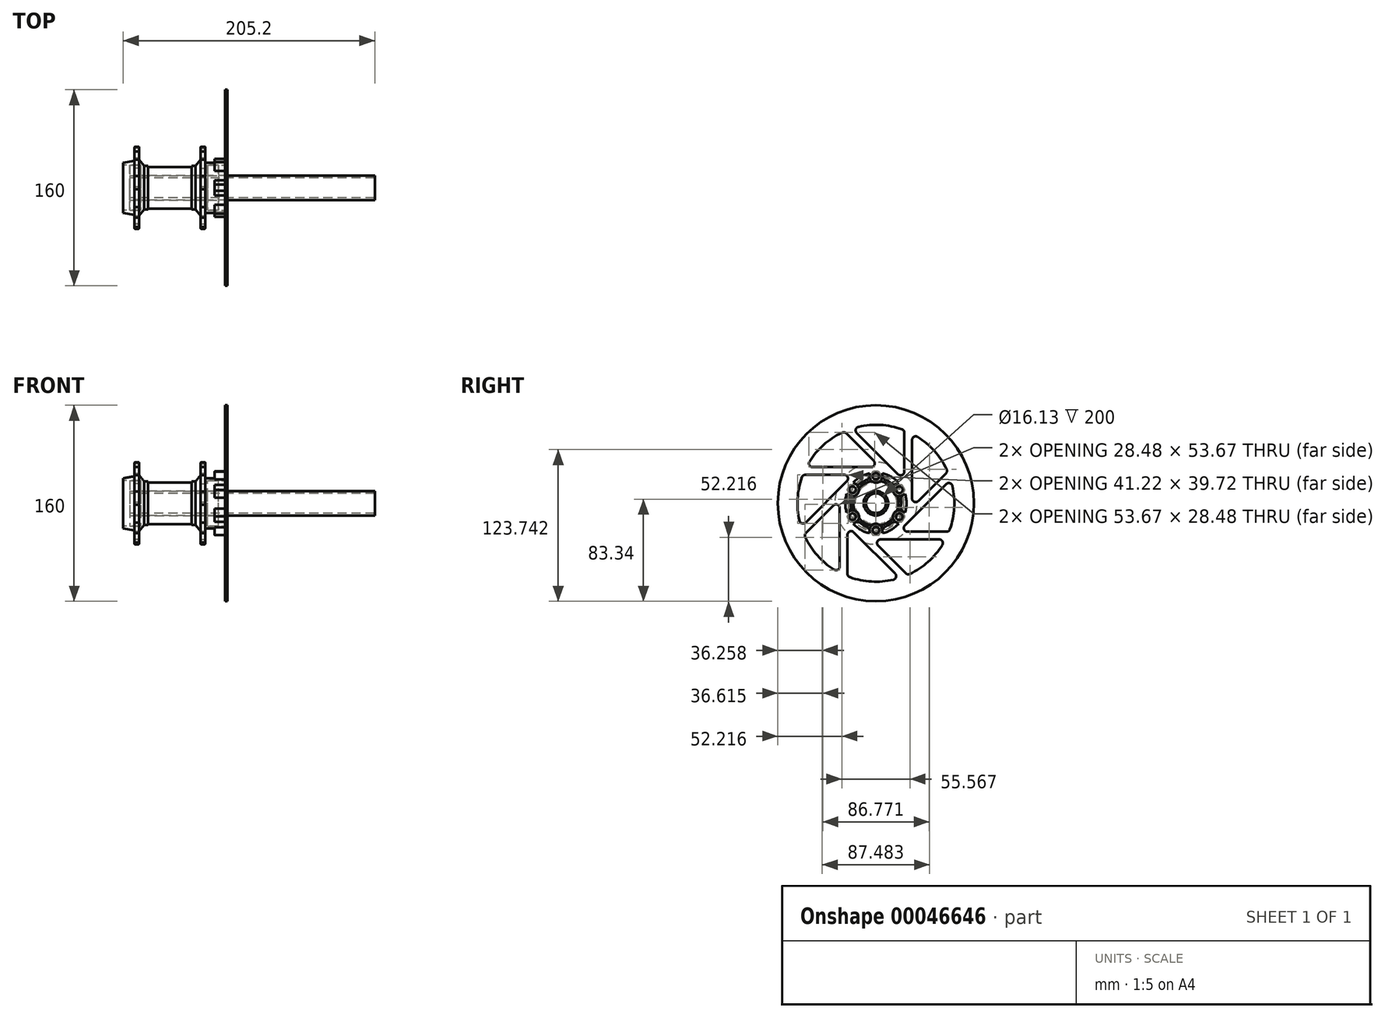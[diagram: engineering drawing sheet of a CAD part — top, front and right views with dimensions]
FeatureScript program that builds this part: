
annotation { "Feature Type Name" : "Feature", "Feature Type Description" : "" }
export const myFeature = defineFeature(function(context is Context, id is Id, definition is map)
    precondition{}
    {
        {
            var Q0;
            Q0=qCreatedBy(makeId("Front.planeOp"),FACE);
            var sketch = newSketch(context, id + "F0", { "sketchPlane" : qUnion([Q0])});
            skLineSegment(sketch, "E0", {"start": v(0, 0) * mm, "end": v(29, 0) * mm});
            skLineSegment(sketch, "E1", {"start": v(29, 0) * mm, "end": v(29, 33.5) * mm});
            skLineSegment(sketch, "E2", {"start": v(29, 33.5) * mm, "end": v(25, 33.5) * mm});
            skLineSegment(sketch, "E3", {"start": v(25, 33.5) * mm, "end": v(25, 17.85) * mm});
            skLineSegment(sketch, "E4", {"start": v(25, 17.85) * mm, "end": v(17.7, 17.85) * mm});
            skLineSegment(sketch, "E5", {"start": v(17.7, 17.85) * mm, "end": v(17.7, 17) * mm});
            skLineSegment(sketch, "E6", {"start": v(17.7, 17) * mm, "end": v(0, 17) * mm});
            skLineSegment(sketch, "E7", {"start": v(0, 17) * mm, "end": v(0, 0) * mm});
            skLineSegment(sketch, "E8", {"start": v(0, 0) * mm, "end": v(0, -15.6) * mm, "construction": true});
            skLineSegment(sketch, "E9", {"start": v(0, 0) * mm, "end": v(-20.97, 0) * mm, "construction": true});
            skSolve(sketch);
        }
        {
            var Q0;
            Q0 = qSketchRegion(id + "F0", true);
            var Q1;
            Q1=sQuery(id+"F0.wireOp",EDGE,"E9");
            revolve(context, id + "F1", {"entities" : qUnion([Q0]), "axis" : qUnion([Q1]), "revolveType" : RevolveType.FULL});
        }
        {
            var Q0;
            Q0=makeQuery(id+"F1.opRevolve","SWEPT_EDGE",EDGE,{"disambiguationData":[OSD([sQuery(id+"F0.wireOp",EDGE,"E3"),sQuery(id+"F0.wireOp",EDGE,"E4")])]});
            chamfer(context, id + "F2", {"entities" : qUnion([Q0]), "chamferType" : ChamferType.TWO_OFFSETS, "width1" : 5 * mm, "oppositeDirection" : false, "width2" : 4 * mm, "tangentPropagation" : true});
        }
        {
            var Q0;
            Q0=makeQuery(id+"F1.opRevolve","SWEPT_EDGE",EDGE,{"disambiguationData":[OSD([sQuery(id+"F0.wireOp",EDGE,"E2"),sQuery(id+"F0.wireOp",EDGE,"E3")])]});
            var Q1;
            Q1=makeQuery(id+"F1.opRevolve","SWEPT_EDGE",EDGE,{"disambiguationData":[OSD([sQuery(id+"F0.wireOp",EDGE,"E1"),sQuery(id+"F0.wireOp",EDGE,"E2")])]});
            fillet(context, id + "F3", {"entities" : qUnion([Q0, Q1]), "radius" : .8 * mm, "tangentPropagation" : true, "allowEdgeOverflow" : false});
        }
        {
            var Q0;
            Q0=makeQuery(id+"F1.opRevolve","SWEPT_BODY",BODY,{"disambiguationData":[OSD([sQuery(id+"F0.wireOp",EDGE,"E0"),sQuery(id+"F0.wireOp",EDGE,"E1"),sQuery(id+"F0.wireOp",EDGE,"E2"),sQuery(id+"F0.wireOp",EDGE,"E3"),sQuery(id+"F0.wireOp",EDGE,"E4"),sQuery(id+"F0.wireOp",EDGE,"E5"),sQuery(id+"F0.wireOp",EDGE,"E6"),sQuery(id+"F0.wireOp",EDGE,"E7")])]});
            var Q1;
            Q1=makeQuery(id+"F1.opRevolve","SWEPT_FACE",FACE,{"disambiguationData":[OSD([sQuery(id+"F0.wireOp",EDGE,"E7")])]});
            mirror(context, id + "F4", {"operationType" : NewBodyOperationType.ADD, "entities" : qUnion([Q0]), "mirrorPlane" : qUnion([Q1])});
        }
        {
            var Q0;
            Q0=makeQuery(id+"F1.opRevolve","SWEPT_FACE",FACE,{"disambiguationData":[OSD([sQuery(id+"F0.wireOp",EDGE,"E1")])]});
            var sketch = newSketch(context, id + "F5", { "sketchPlane" : qUnion([Q0])});
            skCircle(sketch, "E10", {"center": v(0, 0) * mm, "radius": 20.5 * mm});
            skSolve(sketch);
        }
        {
            var Q0;
            Q0 = qSketchRegion(id + "F5", true);
            extrude(context, id + "F6", {"entities" : qUnion([Q0]), "operationType" : NewBodyOperationType.ADD, "depth" : 16 * mm});
        }
        {
            var Q0;
            Q0=makeQuery(id+"F6.opExtrude","CAP_FACE",FACE,{"disambiguationData":[OSD([sQuery(id+"F5.wireOp",EDGE,"E10")])],"isStart":false});
            var sketch = newSketch(context, id + "F7", { "sketchPlane" : qUnion([Q0])});
            skArc(sketch, "E11", {"start": v(2.5, 25.88) * mm, "mid": v(0, 26) * mm, "end": v(-2.5, 25.88) * mm});
            skLineSegment(sketch, "E12", {"start": v(-2.5, 25.88) * mm, "end": v(-17.44, 0) * mm});
            skLineSegment(sketch, "E13", {"start": v(-17.44, 0) * mm, "end": v(17.44, 0) * mm});
            skLineSegment(sketch, "E14", {"start": v(17.44, 0) * mm, "end": v(2.5, 25.88) * mm});
            skLineSegment(sketch, "E15", {"start": v(0, 0) * mm, "end": v(0, 26) * mm, "construction": true});
            skCircle(sketch, "E16", {"center": v(0, 22) * mm, "radius": 2.5 * mm, "construction": true});
            skSolve(sketch);
        }
        {
            var Q0;
            Q0 = qSketchRegion(id + "F7", true);
            extrude(context, id + "F8", {"entities" : qUnion([Q0]), "operationType" : NewBodyOperationType.ADD, "oppositeDirection" : true, "depth" : 8.5 * mm});
        }
        {
            var Q0;
            Q0=makeQuery(id+"F8.opExtrude","SWEPT_BODY",BODY,{"disambiguationData":[OSD([sQuery(id+"F7.wireOp",EDGE,"E11"),sQuery(id+"F7.wireOp",EDGE,"E12"),sQuery(id+"F7.wireOp",EDGE,"E13"),sQuery(id+"F7.wireOp",EDGE,"E14")])]});
            var Q1;
            Q1=makeQuery(id+"F8.opExtrude","SWEPT_FACE",FACE,{"disambiguationData":[OSD([sQuery(id+"F7.wireOp",EDGE,"E12")])]});
            var Q2;
            Q2=makeQuery(id+"F8.opExtrude","SWEPT_FACE",FACE,{"disambiguationData":[OSD([sQuery(id+"F7.wireOp",EDGE,"E11")])]});
            var Q3;
            Q3=makeQuery(id+"F8.opExtrude","CAP_FACE",FACE,{"disambiguationData":[OSD([sQuery(id+"F7.wireOp",EDGE,"E11"),sQuery(id+"F7.wireOp",EDGE,"E12"),sQuery(id+"F7.wireOp",EDGE,"E13"),sQuery(id+"F7.wireOp",EDGE,"E14")])],"isStart":false});
            var Q4;
            Q4=makeQuery(id+"F8.opExtrude","SWEPT_FACE",FACE,{"disambiguationData":[OSD([sQuery(id+"F7.wireOp",EDGE,"E14")])]});
            var Q5;
            Q5=sQuery(id+"F0.wireOp",EDGE,"E0");
            circularPattern(context, id + "F9", {"operationType" : NewBodyOperationType.ADD, "faces" : qUnion([Q1, Q2, Q3, Q4]), "axis" : qUnion([Q5]), "angle" : 360 * degree, "instanceCount" : 6, "equalSpace" : true, "patternType" : PatternType.FACE});
        }
        {
            var Q0;
            Q0=makeQuery(id+"F8.boolean.opBoolean","MERGE",FACE,{"derivedFrom":[makeQuery(id+"F6.opExtrude","CAP_FACE",FACE,{"disambiguationData":[OSD([sQuery(id+"F5.wireOp",EDGE,"E10")])],"isStart":false}),makeQuery(id+"F8.opExtrude","CAP_FACE",FACE,{"disambiguationData":[OSD([sQuery(id+"F7.wireOp",EDGE,"E11"),sQuery(id+"F7.wireOp",EDGE,"E12"),sQuery(id+"F7.wireOp",EDGE,"E13"),sQuery(id+"F7.wireOp",EDGE,"E14")])],"isStart":true})]});
            var sketch = newSketch(context, id + "F10", { "sketchPlane" : qUnion([Q0])});
            skCircle(sketch, "E17", {"center": v(0, 0) * mm, "radius": 18.5 * mm});
            skSolve(sketch);
        }
        {
            var Q0;
            Q0 = qSketchRegion(id + "F10", true);
            extrude(context, id + "F11", {"entities" : qUnion([Q0]), "operationType" : NewBodyOperationType.REMOVE, "oppositeDirection" : true, "depth" : 14.2 * mm});
        }
        {
            var Q0;
            Q0=makeQuery(id+"F11.boolean.opBoolean","COPY",FACE,{"derivedFrom":makeQuery(id+"F11.opExtrude","CAP_FACE",FACE,{"disambiguationData":[OSD([sQuery(id+"F10.wireOp",EDGE,"E17")])],"isStart":false})});
            extrude(context, id + "F12", {"entities" : qUnion([Q0]), "depth" : 9 * mm});
        }
        {
            var Q0;
            Q0=makeQuery(id+"F4.opPattern","COPY",FACE,{"derivedFrom":makeQuery(id+"F1.opRevolve","SWEPT_FACE",FACE,{"disambiguationData":[OSD([sQuery(id+"F0.wireOp",EDGE,"E1")])]}),"instanceName":"1"});
            var sketch = newSketch(context, id + "F13", { "sketchPlane" : qUnion([Q0])});
            skCircle(sketch, "E18", {"center": v(0, 0) * mm, "radius": 22 * mm});
            skSolve(sketch);
        }
        {
            var Q0;
            Q0 = qSketchRegion(id + "F13", true);
            extrude(context, id + "F14", {"entities" : qUnion([Q0]), "operationType" : NewBodyOperationType.ADD, "depth" : 9 * mm, "hasDraft" : true, "draftAngle" : 10 * degree, "draftPullDirection" : true});
        }
        {
            var Q0;
            Q0=makeQuery(id+"F14.opExtrude","CAP_FACE",FACE,{"disambiguationData":[OSD([sQuery(id+"F13.wireOp",EDGE,"E18")])],"isStart":false});
            var sketch = newSketch(context, id + "F15", { "sketchPlane" : qUnion([Q0])});
            skCircle(sketch, "E19", {"center": v(0, 0) * mm, "radius": 18.5 * mm});
            skSolve(sketch);
        }
        {
            var Q0;
            Q0 = qSketchRegion(id + "F15", true);
            extrude(context, id + "F16", {"entities" : qUnion([Q0]), "operationType" : NewBodyOperationType.REMOVE, "oppositeDirection" : true, "depth" : 14.2 * mm});
        }
        {
            var Q0;
            Q0=makeQuery(id+"F16.boolean.opBoolean","COPY",FACE,{"derivedFrom":makeQuery(id+"F16.opExtrude","CAP_FACE",FACE,{"disambiguationData":[OSD([sQuery(id+"F15.wireOp",EDGE,"E19")])],"isStart":false})});
            extrude(context, id + "F17", {"entities" : qUnion([Q0]), "depth" : 9 * mm});
        }
        {
            var Q0;
            Q0=qCreatedBy(makeId("Right.planeOp"),FACE);
            var sketch = newSketch(context, id + "F18", { "sketchPlane" : qUnion([Q0])});
            skCircle(sketch, "E20", {"center": v(0, 0) * mm, "radius": 10 * mm});
            skSolve(sketch);
        }
        {
            var Q0;
            Q0 = qSketchRegion(id + "F18", true);
            extrude(context, id + "F19", {"entities" : qUnion([Q0]), "operationType" : NewBodyOperationType.REMOVE, "endBound" : BoundingType.THROUGH_ALL, "oppositeDirection" : true, "depth" : 25 * mm, "hasSecondDirection" : true, "secondDirectionBound" : SecondDirectionBoundingType.THROUGH_ALL, "secondDirectionOppositeDirection" : false, "secondDirectionDepth" : 25 * mm});
        }
        {
            var Q0;
            Q0=makeQuery(id+"F8.boolean.opBoolean","MERGE",FACE,{"derivedFrom":[makeQuery(id+"F6.opExtrude","CAP_FACE",FACE,{"disambiguationData":[OSD([sQuery(id+"F5.wireOp",EDGE,"E10")])],"isStart":false}),makeQuery(id+"F8.opExtrude","CAP_FACE",FACE,{"disambiguationData":[OSD([sQuery(id+"F7.wireOp",EDGE,"E11"),sQuery(id+"F7.wireOp",EDGE,"E12"),sQuery(id+"F7.wireOp",EDGE,"E13"),sQuery(id+"F7.wireOp",EDGE,"E14")])],"isStart":true})]});
            var sketch = newSketch(context, id + "F20", { "sketchPlane" : qUnion([Q0])});
            skArc(sketch, "E21", {"start": v(-5.25, 24.44) * mm, "mid": v(-8.98, 23.33) * mm, "end": v(-12.5, 21.65) * mm});
            skCircle(sketch, "E22", {"center": v(0, 22) * mm, "radius": 2.7 * mm});
            skArc(sketch, "E23", {"start": v(-5.25, 22) * mm, "mid": v(0, 16.75) * mm, "end": v(5.25, 22) * mm});
            skLineSegment(sketch, "E24", {"start": v(-5.25, 22) * mm, "end": v(-5.25, 24.44) * mm});
            skLineSegment(sketch, "E25", {"start": v(5.25, 22) * mm, "end": v(5.25, 24.44) * mm});
            skLineSegment(sketch, "E26", {"start": v(-40, 69.28) * mm, "end": v(-12.5, 21.65) * mm});
            skLineSegment(sketch, "E27", {"start": v(40, 69.28) * mm, "end": v(12.5, 21.65) * mm});
            skArc(sketch, "E28", {"start": v(40, 69.28) * mm, "mid": v(0, 80) * mm, "end": v(-40, 69.28) * mm});
            skArc(sketch, "E29.trimOffspring", {"start": v(12.5, 21.65) * mm, "mid": v(8.98, 23.33) * mm, "end": v(5.25, 24.44) * mm});
            skSolve(sketch);
        }
        {
            var Q0;
            Q0 = qSketchRegion(id + "F20", true);
            extrude(context, id + "F21", {"entities" : qUnion([Q0]), "depth" : 2 * mm});
        }
        {
            var Q0;
            Q0=makeQuery(id+"F21.opExtrude","SWEPT_BODY",BODY,{"disambiguationData":[OSD([sQuery(id+"F20.wireOp",EDGE,"E21"),sQuery(id+"F20.wireOp",EDGE,"E22"),sQuery(id+"F20.wireOp",EDGE,"E23"),sQuery(id+"F20.wireOp",EDGE,"E24"),sQuery(id+"F20.wireOp",EDGE,"E25"),sQuery(id+"F20.wireOp",EDGE,"E26"),sQuery(id+"F20.wireOp",EDGE,"E27"),sQuery(id+"F20.wireOp",EDGE,"E28"),sQuery(id+"F20.wireOp",EDGE,"E29.trimOffspring")])]});
            var Q1;
            Q1=sQuery(id+"F0.wireOp",EDGE,"E0");
            circularPattern(context, id + "F22", {"operationType" : NewBodyOperationType.ADD, "entities" : qUnion([Q0]), "axis" : qUnion([Q1]), "angle" : 360 * degree, "instanceCount" : 6, "equalSpace" : true});
        }
        {
            var Q0;
            {var subQ0=makeQuery(id+"F21.opExtrude","CAP_FACE",FACE,{"disambiguationData":[OSD([sQuery(id+"F20.wireOp",EDGE,"E21"),sQuery(id+"F20.wireOp",EDGE,"E22"),sQuery(id+"F20.wireOp",EDGE,"E23"),sQuery(id+"F20.wireOp",EDGE,"E24"),sQuery(id+"F20.wireOp",EDGE,"E25"),sQuery(id+"F20.wireOp",EDGE,"E26"),sQuery(id+"F20.wireOp",EDGE,"E27"),sQuery(id+"F20.wireOp",EDGE,"E28"),sQuery(id+"F20.wireOp",EDGE,"E29.trimOffspring")])],"isStart":false});Q0=makeQuery(id+"F22.boolean.opBoolean","MERGE",FACE,{"derivedFrom":[subQ0,makeQuery(id+"F22.opPattern","COPY",FACE,{"derivedFrom":subQ0,"instanceName":"1"}),makeQuery(id+"F22.opPattern","COPY",FACE,{"derivedFrom":subQ0,"instanceName":"2"}),makeQuery(id+"F22.opPattern","COPY",FACE,{"derivedFrom":subQ0,"instanceName":"3"}),makeQuery(id+"F22.opPattern","COPY",FACE,{"derivedFrom":subQ0,"instanceName":"4"}),makeQuery(id+"F22.opPattern","COPY",FACE,{"derivedFrom":subQ0,"instanceName":"5"})]});}
            var sketch = newSketch(context, id + "F23", { "sketchPlane" : qUnion([Q0])});
            skLineSegment(sketch, "E30", {"start": v(-51.62, 29.5) * mm, "end": v(-3.93, 29.5) * mm});
            skLineSegment(sketch, "E31", {"start": v(-1.81, 34.62) * mm, "end": v(-24.3, 57.1) * mm});
            skArc(sketch, "E32", {"start": v(-27.72, 57.69) * mm, "mid": v(-42.6, 47.76) * mm, "end": v(-54.16, 34.1) * mm});
            skPoint(sketch, "E33.visualSharp", {"position": v(3.3, 29.5) * mm});
            skArc(sketch, "E33.filletArc", {"start": v(-3.93, 29.5) * mm, "mid": v(-1.16, 31.35) * mm, "end": v(-1.81, 34.62) * mm});
            skPoint(sketch, "E34.visualSharp", {"position": v(-25.77, 58.58) * mm});
            skArc(sketch, "E34.filletArc", {"start": v(-24.3, 57.1) * mm, "mid": v(-25.91, 57.94) * mm, "end": v(-27.72, 57.69) * mm});
            skPoint(sketch, "E35.visualSharp", {"position": v(-56.8, 29.5) * mm});
            skArc(sketch, "E35.filletArc", {"start": v(-54.16, 34.1) * mm, "mid": v(-54.25, 31.05) * mm, "end": v(-51.62, 29.5) * mm});
            skSolve(sketch);
        }
        {
            var Q0;
            Q0 = qSketchRegion(id + "F23", true);
            extrude(context, id + "F24", {"entities" : qUnion([Q0]), "operationType" : NewBodyOperationType.REMOVE, "endBound" : BoundingType.THROUGH_ALL, "oppositeDirection" : true, "depth" : 25 * mm});
        }
        {
            var Q0;
            Q0=makeQuery(id+"F24.boolean.opBoolean","COPY",FACE,{"derivedFrom":makeQuery(id+"F24.opExtrude","SWEPT_FACE",FACE,{"disambiguationData":[OSD([sQuery(id+"F23.wireOp",EDGE,"E34.filletArc")])]})});
            var Q1;
            Q1=makeQuery(id+"F24.boolean.opBoolean","COPY",FACE,{"derivedFrom":makeQuery(id+"F24.opExtrude","SWEPT_FACE",FACE,{"disambiguationData":[OSD([sQuery(id+"F23.wireOp",EDGE,"E31")])]})});
            var Q2;
            Q2=makeQuery(id+"F24.boolean.opBoolean","COPY",FACE,{"derivedFrom":makeQuery(id+"F24.opExtrude","SWEPT_FACE",FACE,{"disambiguationData":[OSD([sQuery(id+"F23.wireOp",EDGE,"E33.filletArc")])]})});
            var Q3;
            Q3=makeQuery(id+"F24.boolean.opBoolean","COPY",FACE,{"derivedFrom":makeQuery(id+"F24.opExtrude","SWEPT_FACE",FACE,{"disambiguationData":[OSD([sQuery(id+"F23.wireOp",EDGE,"E32")])]})});
            var Q4;
            Q4=makeQuery(id+"F24.boolean.opBoolean","COPY",FACE,{"derivedFrom":makeQuery(id+"F24.opExtrude","SWEPT_FACE",FACE,{"disambiguationData":[OSD([sQuery(id+"F23.wireOp",EDGE,"E35.filletArc")])]})});
            var Q5;
            Q5=makeQuery(id+"F24.boolean.opBoolean","COPY",FACE,{"derivedFrom":makeQuery(id+"F24.opExtrude","SWEPT_FACE",FACE,{"disambiguationData":[OSD([sQuery(id+"F23.wireOp",EDGE,"E30")])]})});
            var Q6;
            Q6=sQuery(id+"F0.wireOp",EDGE,"E0");
            circularPattern(context, id + "F25", {"faces" : qUnion([Q0, Q1, Q2, Q3, Q4, Q5]), "axis" : qUnion([Q6]), "angle" : 360 * degree, "instanceCount" : 8, "equalSpace" : true, "patternType" : PatternType.FACE});
        }
        {
            var Q0;
            Q0=makeQuery(id+"F17.opExtrude","CAP_FACE",FACE,{"disambiguationData":[OSD([sQuery(id+"F15.wireOp",EDGE,"E19")])],"isStart":false});
            var sketch = newSketch(context, id + "F26", { "sketchPlane" : qUnion([Q0])});
            skCircle(sketch, "E36", {"center": v(0, 0) * mm, "radius": 9.95 * mm});
            skCircle(sketch, "E37", {"center": v(0, 0) * mm, "radius": 8.06 * mm});
            skSolve(sketch);
        }
        {
            var Q0;
            Q0 = qSketchRegion(id + "F26", true);
            extrude(context, id + "F27", {"entities" : qUnion([Q0]), "oppositeDirection" : true, "depth" : 200 * mm});
        }
    });
